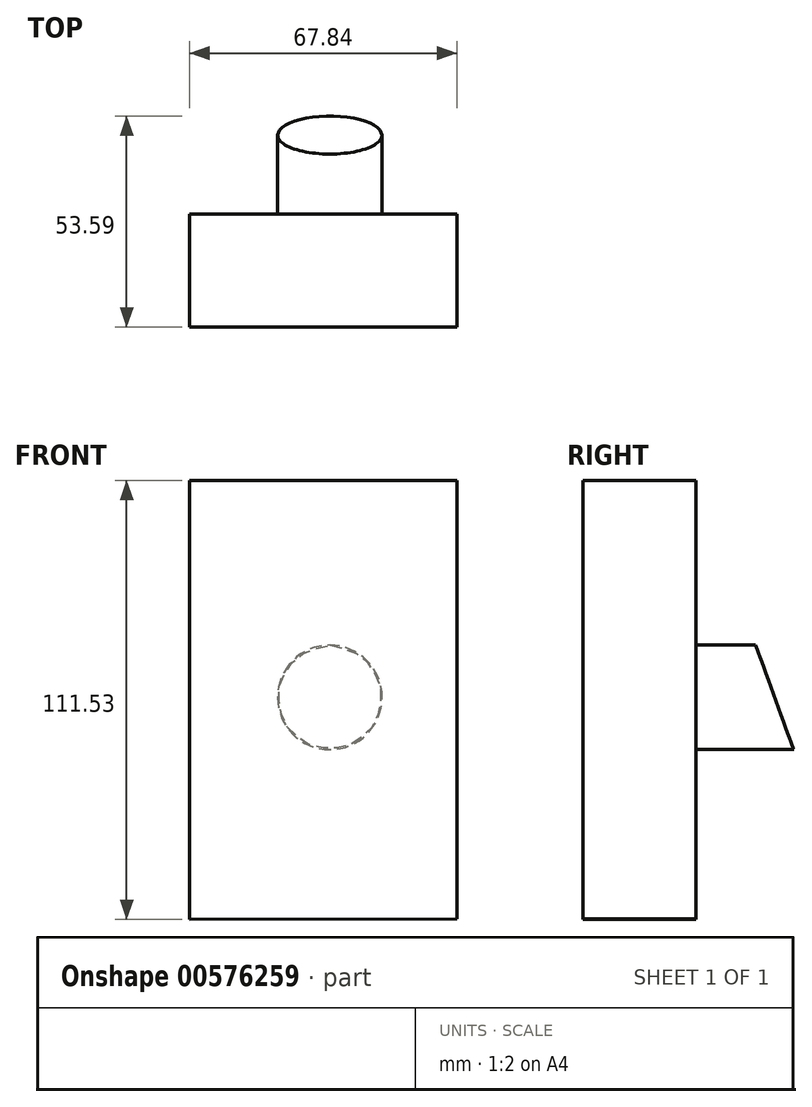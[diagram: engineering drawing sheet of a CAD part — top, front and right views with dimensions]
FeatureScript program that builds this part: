
annotation { "Feature Type Name" : "Feature", "Feature Type Description" : "" }
export const myFeature = defineFeature(function(context is Context, id is Id, definition is map)
    precondition{}
    {
        {
            var Q0;
            Q0=qCreatedBy(makeId("Front.planeOp"),FACE);
            var sketch = newSketch(context, id + "F0", { "sketchPlane" : qUnion([Q0])});
            skLineSegment(sketch, "E0", {"start": v(-35.58, 55.12) * mm, "end": v(-35.58, -56.41) * mm});
            skLineSegment(sketch, "E1", {"start": v(-35.58, 55.12) * mm, "end": v(32.26, 55.12) * mm});
            skLineSegment(sketch, "E2", {"start": v(32.26, 55.12) * mm, "end": v(32.26, -56.23) * mm});
            skLineSegment(sketch, "E3", {"start": v(32.26, -56.23) * mm, "end": v(-35.58, -56.41) * mm});
            skSolve(sketch);
        }
        {
            var Q0;
            Q0=makeQuery(id+"F0.imprint","IMPRINT",FACE,{"disambiguationData":[TD([[makeQuery(id+"F0.imprint","IMPRINT",EDGE,{"derivedFrom":sQuery(id+"F0.wireOp",EDGE,"E0")}),1.0]])]});
            extrude(context, id + "F1", {"entities" : qUnion([Q0]), "oppositeDirection" : true, "depth" : 28.7 * mm, "offsetDistance" : 25.4 * mm});
        }
        {
            var Q0;
            Q0=makeQuery(id+"F1.opExtrude","CAP_EDGE",EDGE,{"disambiguationData":[OSD([sQuery(id+"F0.wireOp",EDGE,"E1")])],"isStart":false});
            cPlane(context, id + "F2", {"entities" : qUnion([Q0]), "cplaneType" : CPlaneType.LINE_ANGLE, "offset" : 25.4 * mm, "angle" : 20 * degree, "width" : 152.4 * mm, "height" : 152.4 * mm});
        }
        {
            var Q0;
            Q0=makeQuery(id+"F1.opExtrude","CAP_FACE",FACE,{"disambiguationData":[OSD([sQuery(id+"F0.wireOp",EDGE,"E0"),sQuery(id+"F0.wireOp",EDGE,"E1"),sQuery(id+"F0.wireOp",EDGE,"E2"),sQuery(id+"F0.wireOp",EDGE,"E3")])],"isStart":false});
            var sketch = newSketch(context, id + "F3", { "sketchPlane" : qUnion([Q0])});
            skCircle(sketch, "E4", {"center": v(0, 0) * mm, "radius": 13.27 * mm});
            skSolve(sketch);
        }
        {
            var Q0;
            Q0=makeQuery(id+"F3.imprint","IMPRINT",FACE,{"disambiguationData":[TD([[makeQuery(id+"F3.imprint","IMPRINT",EDGE,{"derivedFrom":sQuery(id+"F3.wireOp",EDGE,"E4")}),1.0]])]});
            var Q1;
            Q1=qCreatedBy(id+"F2.planeOp",FACE);
            extrude(context, id + "F4", {"entities" : qUnion([Q0]), "operationType" : NewBodyOperationType.ADD, "endBound" : BoundingType.UP_TO_SURFACE, "depth" : 34.3 * mm, "endBoundEntityFace" : qUnion([Q1]), "offsetDistance" : 25.4 * mm});
        }
    });
